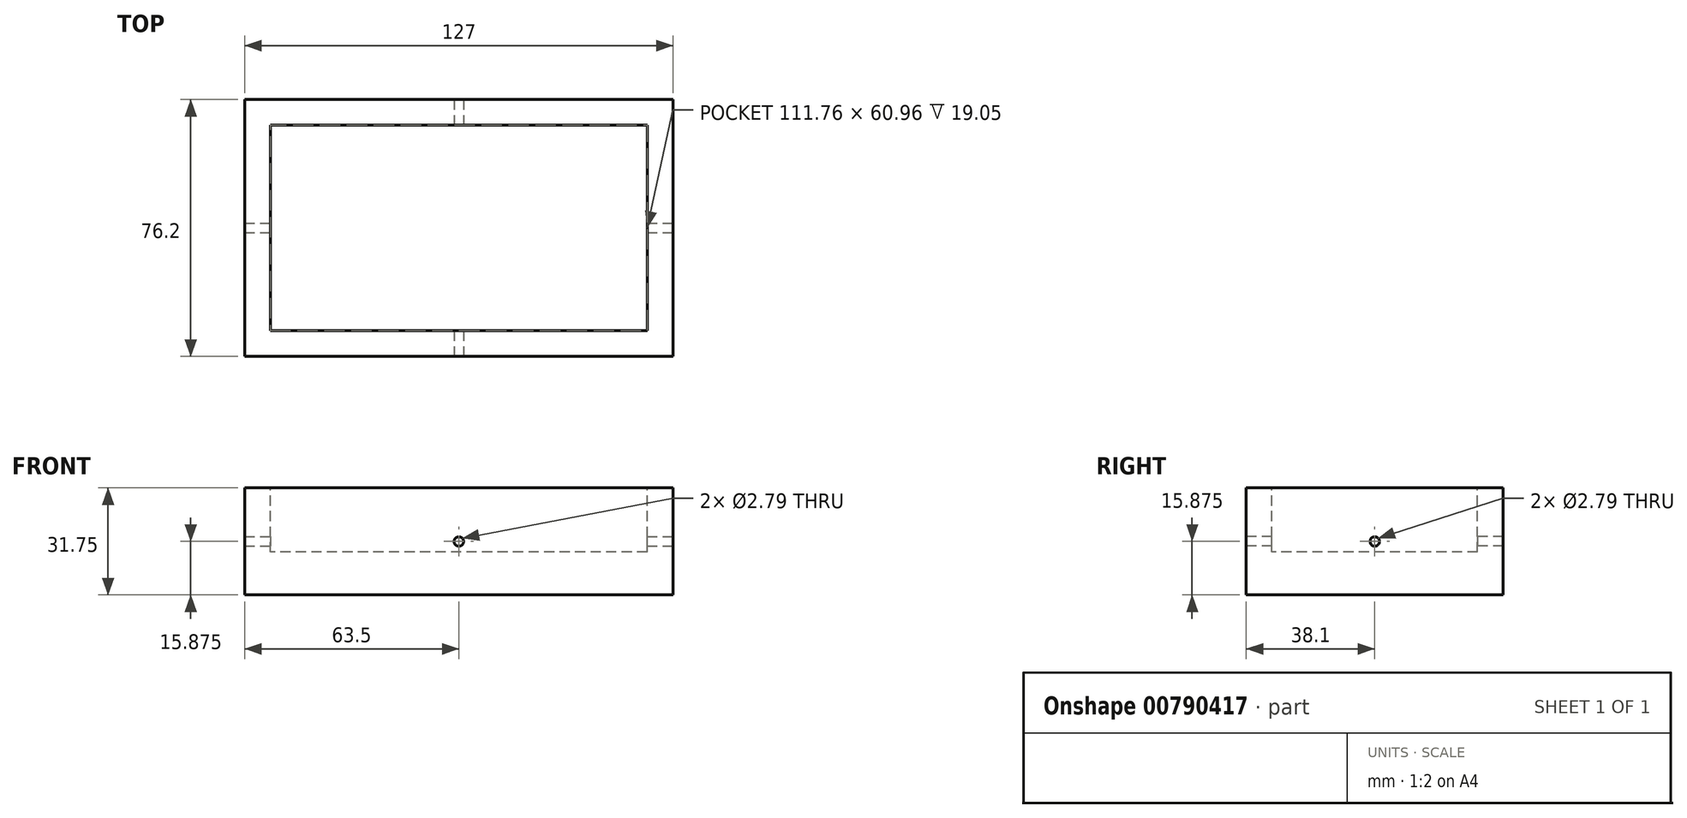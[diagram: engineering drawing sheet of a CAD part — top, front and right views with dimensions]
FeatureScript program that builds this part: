
annotation { "Feature Type Name" : "Feature", "Feature Type Description" : "" }
export const myFeature = defineFeature(function(context is Context, id is Id, definition is map)
    precondition{}
    {
        {
            var Q0;
            Q0=qCreatedBy(makeId("Top.planeOp"),FACE);
            var sketch = newSketch(context, id + "F0", { "sketchPlane" : qUnion([Q0])});
            skLineSegment(sketch, "E0", {"start": v(0, 0) * mm, "end": v(-63.5, 0) * mm});
            skLineSegment(sketch, "E1", {"start": v(-63.5, 0) * mm, "end": v(-63.5, -76.2) * mm});
            skLineSegment(sketch, "E2", {"start": v(-63.5, -76.2) * mm, "end": v(63.5, -76.2) * mm});
            skLineSegment(sketch, "E3", {"start": v(63.5, -76.2) * mm, "end": v(63.5, 0) * mm});
            skLineSegment(sketch, "E4", {"start": v(63.5, 0) * mm, "end": v(0, 0) * mm});
            skSolve(sketch);
        }
        {
            var Q0;
            Q0=makeQuery(id+"F0.imprint","IMPRINT",FACE,{"disambiguationData":[TD([[makeQuery(id+"F0.imprint","IMPRINT",EDGE,{"derivedFrom":sQuery(id+"F0.wireOp",EDGE,"E0")}),1.0]])]});
            extrude(context, id + "F1", {"entities" : qUnion([Q0]), "depth" : 31.75 * mm, "offsetDistance" : 25.4 * mm});
        }
        {
            var Q0;
            Q0=makeQuery(id+"F1.opExtrude","CAP_FACE",FACE,{"disambiguationData":[OSD([sQuery(id+"F0.wireOp",EDGE,"E0"),sQuery(id+"F0.wireOp",EDGE,"E1"),sQuery(id+"F0.wireOp",EDGE,"E2"),sQuery(id+"F0.wireOp",EDGE,"E3"),sQuery(id+"F0.wireOp",EDGE,"E4")])],"isStart":false});
            var sketch = newSketch(context, id + "F2", { "sketchPlane" : qUnion([Q0])});
            skLineSegment(sketch, "E5", {"start": v(-63.5, -7.62) * mm, "end": v(-55.88, -7.62) * mm, "construction": true});
            skLineSegment(sketch, "E6", {"start": v(-55.88, -7.62) * mm, "end": v(-55.88, 0) * mm, "construction": true});
            skLineSegment(sketch, "E7", {"start": v(-55.88, -7.62) * mm, "end": v(-55.88, -68.58) * mm});
            skLineSegment(sketch, "E8", {"start": v(-55.88, -68.58) * mm, "end": v(55.88, -68.58) * mm});
            skLineSegment(sketch, "E9", {"start": v(55.88, -68.58) * mm, "end": v(55.88, -7.62) * mm});
            skLineSegment(sketch, "E10", {"start": v(55.88, -7.62) * mm, "end": v(-55.88, -7.62) * mm});
            skLineSegment(sketch, "E11", {"start": v(-55.88, -68.58) * mm, "end": v(-55.88, -76.2) * mm, "construction": true});
            skLineSegment(sketch, "E12", {"start": v(55.88, -68.58) * mm, "end": v(63.5, -68.58) * mm, "construction": true});
            skSolve(sketch);
        }
        {
            var Q0;
            Q0=makeQuery(id+"F2.imprint","IMPRINT",FACE,{"disambiguationData":[TD([[makeQuery(id+"F2.imprint","IMPRINT",EDGE,{"derivedFrom":sQuery(id+"F2.wireOp",EDGE,"E7")}),1.0]])]});
            extrude(context, id + "F3", {"entities" : qUnion([Q0]), "operationType" : NewBodyOperationType.REMOVE, "oppositeDirection" : true, "depth" : 19.05 * mm, "offsetDistance" : 25.4 * mm});
        }
        {
            var Q0;
            Q0=makeQuery(id+"F1.opExtrude","SWEPT_FACE",FACE,{"disambiguationData":[OSD([sQuery(id+"F0.wireOp",EDGE,"E3")])]});
            var sketch = newSketch(context, id + "F4", { "sketchPlane" : qUnion([Q0])});
            skCircle(sketch, "E13", {"center": v(-38.1, 15.88) * mm, "radius": 1.4 * mm});
            skPoint(sketch, "E13.centerSnap0", {"position": v(0, 15.88) * mm});
            skPoint(sketch, "E13.centerSnap1", {"position": v(-38.1, 31.75) * mm});
            skSolve(sketch);
        }
        {
            var Q0;
            Q0=makeQuery(id+"F4.imprint","IMPRINT",FACE,{"disambiguationData":[TD([[makeQuery(id+"F4.imprint","IMPRINT",EDGE,{"derivedFrom":sQuery(id+"F4.wireOp",EDGE,"E13")}),1.0]])]});
            extrude(context, id + "F5", {"entities" : qUnion([Q0]), "operationType" : NewBodyOperationType.REMOVE, "endBound" : BoundingType.THROUGH_ALL, "oppositeDirection" : true, "depth" : 25.4 * mm, "offsetDistance" : 25.4 * mm});
        }
        {
            var Q0;
            Q0=makeQuery(id+"F1.opExtrude","SWEPT_FACE",FACE,{"disambiguationData":[OSD([sQuery(id+"F0.wireOp",EDGE,"E2")])]});
            var sketch = newSketch(context, id + "F6", { "sketchPlane" : qUnion([Q0])});
            skCircle(sketch, "E14", {"center": v(0, 15.88) * mm, "radius": 1.4 * mm});
            skPoint(sketch, "E14.centerSnap0", {"position": v(63.5, 15.88) * mm});
            skPoint(sketch, "E14.centerSnap1", {"position": v(0, 31.75) * mm});
            skSolve(sketch);
        }
        {
            var Q0;
            Q0=makeQuery(id+"F6.imprint","IMPRINT",FACE,{"disambiguationData":[TD([[makeQuery(id+"F6.imprint","IMPRINT",EDGE,{"derivedFrom":sQuery(id+"F6.wireOp",EDGE,"E14")}),1.0]])]});
            extrude(context, id + "F7", {"entities" : qUnion([Q0]), "operationType" : NewBodyOperationType.REMOVE, "endBound" : BoundingType.THROUGH_ALL, "oppositeDirection" : true, "depth" : 25.4 * mm, "offsetDistance" : 25.4 * mm});
        }
    });
